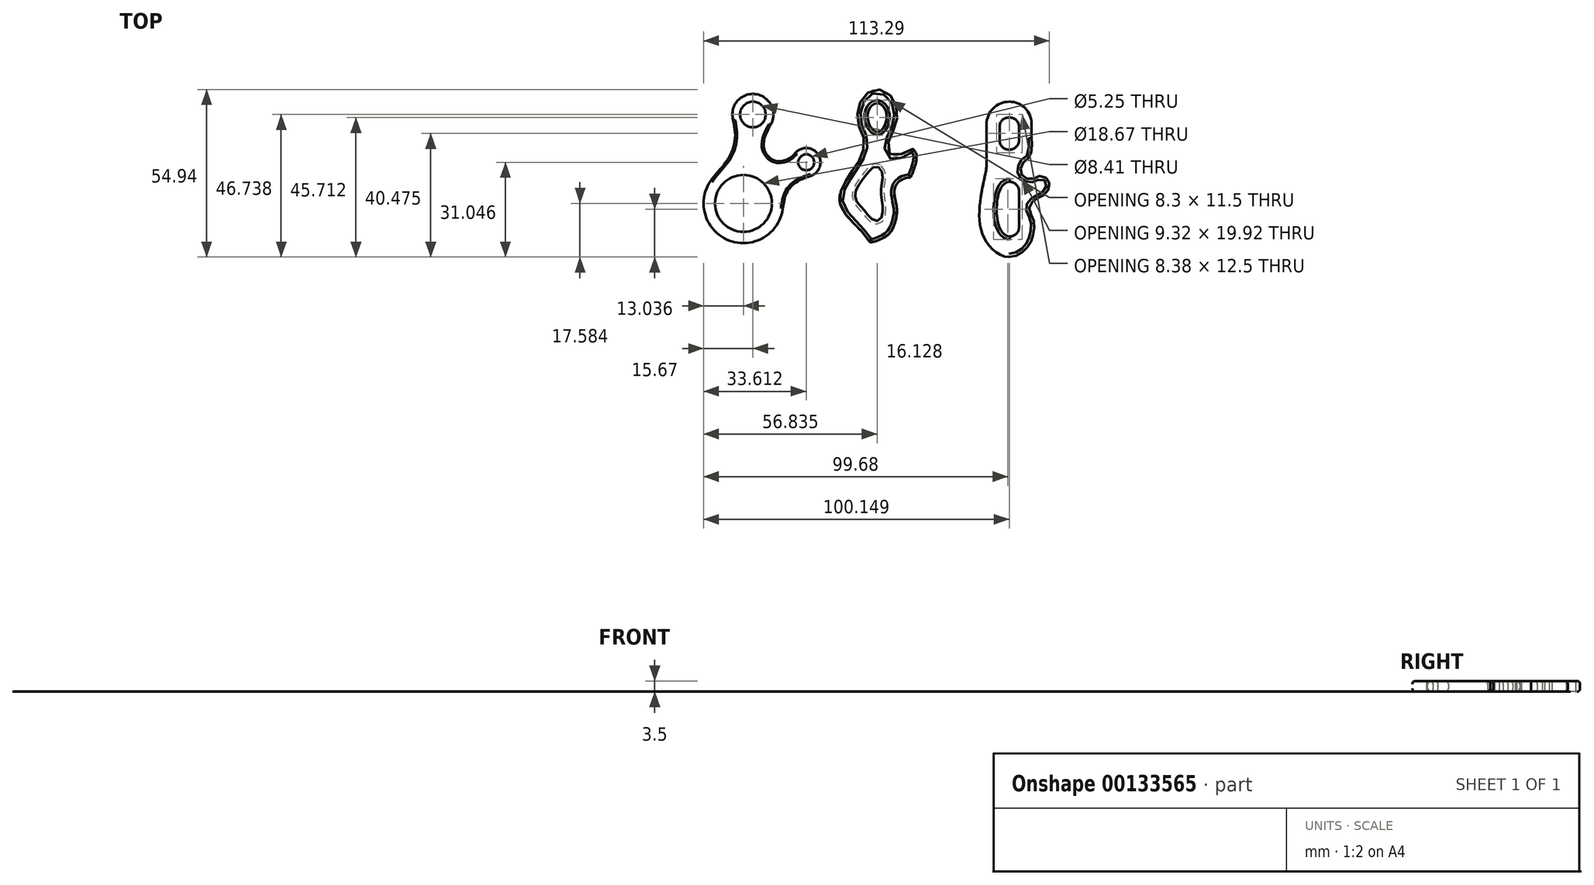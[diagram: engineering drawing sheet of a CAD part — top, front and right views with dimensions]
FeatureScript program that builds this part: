
annotation { "Feature Type Name" : "Feature", "Feature Type Description" : "" }
export const myFeature = defineFeature(function(context is Context, id is Id, definition is map)
    precondition{}
    {
        {
            var Q0;
            Q0=qCreatedBy(makeId("Top.planeOp"),FACE);
            var sketch = newSketch(context, id + "F0", { "sketchPlane" : qUnion([Q0])});
            skCircle(sketch, "E0", {"center": v(-42.03, 15.95) * mm, "radius": 6.72 * mm});
            skPoint(sketch, "E0.first.point", {"position": v(-46.63, 20.85) * mm});
            skPoint(sketch, "E0.second.point", {"position": v(-35.31, 16.12) * mm});
            skPoint(sketch, "E0.third.point", {"position": v(-44.96, 9.9) * mm});
            skCircle(sketch, "E1", {"center": v(-24.55, 0.26) * mm, "radius": 4.69 * mm});
            skPoint(sketch, "E1.first.point", {"position": v(-24.44, 4.94) * mm});
            skPoint(sketch, "E1.second.point", {"position": v(-20.45, -2.01) * mm});
            skPoint(sketch, "E1.third.point", {"position": v(-28.32, -2.52) * mm});
            skCircle(sketch, "E2", {"center": v(-45.12, -13.2) * mm, "radius": 13.03 * mm});
            skPoint(sketch, "E2.first.point", {"position": v(-53.96, -3.63) * mm});
            skPoint(sketch, "E2.second.point", {"position": v(-34.15, -6.18) * mm});
            skPoint(sketch, "E2.third.point", {"position": v(-44.85, -26.24) * mm});
            skFitSpline(sketch, "E3", {"points": [v(-36, 12.97) * mm, v(-38.34, 7.7) * mm, v(-38, 3.62) * mm, v(-34.68, 0.76) * mm, v(-30.27, 1.45) * mm, v(-28, 3.42) * mm], "startDerivative": vector(-12.5, -23.13) * mm, "endDerivative": vector(11.46, 12.78) * mm});
            skFitSpline(sketch, "E4", {"points": [v(-23.1, -4.2) * mm, v(-27.58, -6.11) * mm, v(-30.9, -9.6) * mm, v(-32.22, -15.03) * mm], "startDerivative": vector(-14.25, -4.87) * mm, "endDerivative": vector(-2.28, -16.5) * mm});
            skFitSpline(sketch, "E5", {"points": [v(-48.66, 14.85) * mm, v(-47.85, 8.2) * mm, v(-50.2, 1.33) * mm, v(-55.94, -5.93) * mm], "startDerivative": vector(5.63, -23.91) * mm, "endDerivative": vector(-12.16, -18.24) * mm});
            skCircle(sketch, "E6", {"center": v(-45.12, -13.2) * mm, "radius": 9.34 * mm});
            skCircle(sketch, "E7", {"center": v(-24.55, 0.26) * mm, "radius": 2.63 * mm});
            skCircle(sketch, "E8", {"center": v(-42.03, 15.95) * mm, "radius": 4.2 * mm});
            skSolve(sketch);
        }
        {
            var Q0;
            {var subQ0=sQuery(id+"F0.wireOp",EDGE,"E5");var subQ1=sQuery(id+"F0.wireOp",EDGE,"E0");var subQ2=makeQuery(id+"F0.imprint","INTERSECT",VERTEX,{"disambiguationData":[OD(0.0)],"derivedFrom":[subQ1,subQ0]});Q0=makeQuery(id+"F0.imprint","IMPRINT",FACE,{"disambiguationData":[TD([[makeQuery(id+"F0.imprint","IMPRINT",EDGE,{"disambiguationData":[TD([[subQ2,-1.0]])],"derivedFrom":subQ1}),1.0]])]});}
            var Q1;
            {var subQ0=sQuery(id+"F0.wireOp",EDGE,"E3");var subQ1=sQuery(id+"F0.wireOp",EDGE,"E0");var subQ2=makeQuery(id+"F0.imprint","INTERSECT",VERTEX,{"disambiguationData":[OD(0.0)],"derivedFrom":[subQ1,subQ0]});Q1=makeQuery(id+"F0.imprint","IMPRINT",FACE,{"disambiguationData":[TD([[makeQuery(id+"F0.imprint","IMPRINT",EDGE,{"disambiguationData":[TD([[subQ2,1.0]])],"derivedFrom":subQ1}),1.0]])]});}
            var Q2;
            {var subQ0=sQuery(id+"F0.wireOp",EDGE,"E3");var subQ1=sQuery(id+"F0.wireOp",EDGE,"E1");var subQ2=makeQuery(id+"F0.imprint","INTERSECT",VERTEX,{"disambiguationData":[OD(0.0)],"derivedFrom":[subQ1,subQ0]});Q2=makeQuery(id+"F0.imprint","IMPRINT",FACE,{"disambiguationData":[TD([[makeQuery(id+"F0.imprint","IMPRINT",EDGE,{"disambiguationData":[TD([[subQ2,-1.0]])],"derivedFrom":subQ1}),1.0]])]});}
            var Q3;
            {var subQ0=sQuery(id+"F0.wireOp",EDGE,"E4");var subQ1=sQuery(id+"F0.wireOp",EDGE,"E2");var subQ2=makeQuery(id+"F0.imprint","INTERSECT",VERTEX,{"disambiguationData":[OD(0.0)],"derivedFrom":[subQ1,subQ0]});Q3=makeQuery(id+"F0.imprint","IMPRINT",FACE,{"disambiguationData":[TD([[makeQuery(id+"F0.imprint","IMPRINT",EDGE,{"disambiguationData":[TD([[subQ2,-1.0]])],"derivedFrom":subQ1}),1.0]])]});}
            var Q4;
            Q4=makeQuery(id+"F0.imprint","IMPRINT",FACE,{"disambiguationData":[TD([[makeQuery(id+"F0.imprint","IMPRINT",EDGE,{"derivedFrom":sQuery(id+"F0.wireOp",EDGE,"E7")}),-1.0]])]});
            var Q5;
            Q5=makeQuery(id+"F0.imprint","IMPRINT",FACE,{"disambiguationData":[TD([[makeQuery(id+"F0.imprint","IMPRINT",EDGE,{"derivedFrom":sQuery(id+"F0.wireOp",EDGE,"E6")}),-1.0]])]});
            var Q6;
            Q6=makeQuery(id+"F0.imprint","IMPRINT",FACE,{"disambiguationData":[TD([[makeQuery(id+"F0.imprint","IMPRINT",EDGE,{"derivedFrom":sQuery(id+"F0.wireOp",EDGE,"E8")}),-1.0]])]});
            var Q7;
            {var subQ1=sQuery(id+"F0.wireOp",EDGE,"E0");var subQ5=sQuery(id+"F0.wireOp",EDGE,"E5");var subQ11=makeQuery(id+"F0.imprint","INTERSECT",VERTEX,{"disambiguationData":[OD(1.0)],"derivedFrom":[subQ1,subQ5]});Q7=makeQuery(id+"F0.imprint","IMPRINT",FACE,{"disambiguationData":[TD([[makeQuery(id+"F0.imprint","IMPRINT",EDGE,{"disambiguationData":[TD([[subQ11,-1.0]])],"derivedFrom":subQ1}),-1.0]])]});}
            extrude(context, id + "F1", {"entities" : qUnion([Q0, Q1, Q2, Q3, Q4, Q5, Q6, Q7]), "depth" : 3.5 * mm});
        }
        {
            var Q0;
            Q0=makeQuery(id+"F1.opExtrude","CAP_FACE",FACE,{"disambiguationData":[OSD([sQuery(id+"F0.wireOp",EDGE,"E0"),sQuery(id+"F0.wireOp",EDGE,"E1"),sQuery(id+"F0.wireOp",EDGE,"E2"),sQuery(id+"F0.wireOp",EDGE,"E3"),sQuery(id+"F0.wireOp",EDGE,"E4"),sQuery(id+"F0.wireOp",EDGE,"E5"),sQuery(id+"F0.wireOp",EDGE,"E6"),sQuery(id+"F0.wireOp",EDGE,"E7"),sQuery(id+"F0.wireOp",EDGE,"E8")])],"isStart":false});
            var Q1;
            Q1=makeQuery(id+"F1.opExtrude","CAP_FACE",FACE,{"disambiguationData":[OSD([sQuery(id+"F0.wireOp",EDGE,"E0"),sQuery(id+"F0.wireOp",EDGE,"E1"),sQuery(id+"F0.wireOp",EDGE,"E2"),sQuery(id+"F0.wireOp",EDGE,"E3"),sQuery(id+"F0.wireOp",EDGE,"E4"),sQuery(id+"F0.wireOp",EDGE,"E5"),sQuery(id+"F0.wireOp",EDGE,"E6"),sQuery(id+"F0.wireOp",EDGE,"E7"),sQuery(id+"F0.wireOp",EDGE,"E8")])],"isStart":true});
            fillet(context, id + "F2", {"entities" : qUnion([Q0, Q1]), "radius" : 0.6 * mm, "tangentPropagation" : true, "allowEdgeOverflow" : false});
        }
        {
            var Q0;
            Q0=qCreatedBy(makeId("Top.planeOp"),FACE);
            var sketch = newSketch(context, id + "F3", { "sketchPlane" : qUnion([Q0])});
            skFitSpline(sketch, "E9", {"points": [v(-0.97, 24.13) * mm, v(3.88, 21.07) * mm, v(5.05, 13.74) * mm, v(2.71, 7.82) * mm, v(2.22, 4.17) * mm, v(3.5, 2.34) * mm, v(5.5, 2.26) * mm, v(7.4, 3.58) * mm, v(9.27, 4.44) * mm, v(10.25, 4.56) * mm, v(10.56, 4.56) * mm, v(10.87, 4.13) * mm, v(11.62, 1.8) * mm, v(9.66, -4.56) * mm, v(9.31, -4.67) * mm, v(5.53, -6.23) * mm, v(4.4, -10.79) * mm, v(5.14, -15.04) * mm, v(4.29, -20.3) * mm, v(1.52, -24.07) * mm, v(-2.8, -25.87) * mm, v(-3.7, -25.87) * mm, v(-4.36, -24.9) * mm, v(-7.56, -21.2) * mm, v(-12.04, -16.17) * mm, v(-13.55, -10.95) * mm, v(-10.09, -3.43) * mm, v(-6.7, 1.8) * mm, v(-5.5, 7.28) * mm, v(-6.7, 10.71) * mm, v(-7.8, 15.74) * mm, v(-5.38, 22.2) * mm, v(-0.97, 24.13) * mm]});
            skFitSpline(sketch, "E10", {"points": [v(-1.25, 19.67) * mm, v(1.83, 15.5) * mm, v(-1.2, 10.17) * mm, v(-4.48, 15.7) * mm, v(-1.25, 19.67) * mm]});
            skFitSpline(sketch, "E11", {"points": [v(-0.86, -1.32) * mm, v(0.47, -3.82) * mm, v(0, -8.76) * mm, v(0.5, -16.48) * mm, v(-1.01, -18.93) * mm, v(-3.15, -18.27) * mm, v(-5.57, -15.43) * mm, v(-7.99, -12.58) * mm, v(-8.26, -9) * mm, v(-5.92, -5.26) * mm, v(-3.62, -2.34) * mm, v(-1.9, -1.13) * mm, v(-0.86, -1.32) * mm]});
            skSolve(sketch);
        }
        {
            var Q0;
            Q0=makeQuery(id+"F3.imprint","IMPRINT",FACE,{"disambiguationData":[TD([[makeQuery(id+"F3.imprint","IMPRINT",EDGE,{"derivedFrom":sQuery(id+"F3.wireOp",EDGE,"E9")}),-1.0]])]});
            extrude(context, id + "F4", {"entities" : qUnion([Q0]), "depth" : 3.5 * mm});
        }
        {
            var Q0;
            Q0=makeQuery(id+"F4.opExtrude","CAP_FACE",FACE,{"disambiguationData":[OSD([sQuery(id+"F3.wireOp",EDGE,"E9"),sQuery(id+"F3.wireOp",EDGE,"E10"),sQuery(id+"F3.wireOp",EDGE,"E11")])],"isStart":true});
            var Q1;
            Q1=makeQuery(id+"F4.opExtrude","CAP_FACE",FACE,{"disambiguationData":[OSD([sQuery(id+"F3.wireOp",EDGE,"E9"),sQuery(id+"F3.wireOp",EDGE,"E10"),sQuery(id+"F3.wireOp",EDGE,"E11")])],"isStart":false});
            fillet(context, id + "F5", {"entities" : qUnion([Q0, Q1]), "radius" : 1 * mm, "tangentPropagation" : true, "allowEdgeOverflow" : false});
        }
        {
            var Q0;
            Q0=qCreatedBy(makeId("Top.planeOp"),FACE);
            var sketch = newSketch(context, id + "F6", { "sketchPlane" : qUnion([Q0])});
            skLineSegment(sketch, "E12.bottom", {"start": v(41.8, 14.94) * mm, "end": v(42.18, 14.94) * mm});
            skLineSegment(sketch, "E12.top", {"start": v(41.8, 4.43) * mm, "end": v(42.18, 4.43) * mm});
            skLineSegment(sketch, "E12.left", {"start": v(38.8, 11.94) * mm, "end": v(38.8, 7.43) * mm});
            skLineSegment(sketch, "E12.right", {"start": v(45.18, 11.94) * mm, "end": v(45.18, 7.43) * mm});
            skLineSegment(sketch, "E13.left", {"start": v(45.18, -9.16) * mm, "end": v(45.18, -21.08) * mm});
            skPoint(sketch, "E14.visualSharp", {"position": v(45.18, 14.94) * mm});
            skArc(sketch, "E14.filletArc", {"start": v(45.18, 11.94) * mm, "mid": v(44.3, 14.06) * mm, "end": v(42.18, 14.94) * mm});
            skPoint(sketch, "E15.visualSharp", {"position": v(38.8, 4.43) * mm});
            skArc(sketch, "E15.filletArc", {"start": v(38.8, 7.43) * mm, "mid": v(39.68, 5.31) * mm, "end": v(41.8, 4.43) * mm});
            skPoint(sketch, "E16.visualSharp", {"position": v(38.8, 14.94) * mm});
            skArc(sketch, "E16.filletArc", {"start": v(41.8, 14.94) * mm, "mid": v(39.68, 14.06) * mm, "end": v(38.8, 11.94) * mm});
            skPoint(sketch, "E17.visualSharp", {"position": v(45.18, 4.43) * mm});
            skArc(sketch, "E17.filletArc", {"start": v(42.18, 4.43) * mm, "mid": v(44.3, 5.31) * mm, "end": v(45.18, 7.43) * mm});
            skPoint(sketch, "E18.visualSharp", {"position": v(45.18, -6.16) * mm});
            skArc(sketch, "E18.filletArc", {"start": v(45.18, -9.16) * mm, "mid": v(44.3, -7.04) * mm, "end": v(42.18, -6.16) * mm});
            skPoint(sketch, "E19.visualSharp", {"position": v(45.18, -24.08) * mm});
            skArc(sketch, "E19.filletArc", {"start": v(42.18, -24.08) * mm, "mid": v(44.3, -23.2) * mm, "end": v(45.18, -21.08) * mm});
            skPoint(sketch, "E20.visualSharp", {"position": v(37.86, -24.08) * mm});
            skPoint(sketch, "E21.visualSharp", {"position": v(37.86, -6.16) * mm});
            skFitSpline(sketch, "E22", {"points": [v(42.18, -6.16) * mm, v(40, -7.04) * mm, v(38.37, -10.56) * mm, v(37.86, -15.54) * mm, v(39.15, -21.85) * mm, v(42.18, -24.08) * mm], "startDerivative": vector(-16.44, -0.23) * mm, "endDerivative": vector(17.29, -0.61) * mm});
            skLineSegment(sketch, "E23.bottom", {"start": v(42.03, 20.13) * mm, "end": v(42.13, 20.13) * mm});
            skLineSegment(sketch, "E23.top", {"start": v(41.91, -30.8) * mm, "end": v(41.95, -30.8) * mm});
            skLineSegment(sketch, "E23.left", {"start": v(34.53, 12.63) * mm, "end": v(34.53, -0.55) * mm});
            skLineSegment(sketch, "E23.right", {"start": v(49.27, 12.98) * mm, "end": v(49.27, 8.16) * mm});
            skPoint(sketch, "E24.visualSharp", {"position": v(34.53, 20.13) * mm});
            skArc(sketch, "E24.filletArc", {"start": v(42.03, 20.13) * mm, "mid": v(36.73, 17.93) * mm, "end": v(34.53, 12.63) * mm});
            skPoint(sketch, "E25.visualSharp", {"position": v(49.27, 20.13) * mm});
            skArc(sketch, "E25.filletArc", {"start": v(49.27, 12.98) * mm, "mid": v(47.18, 18.03) * mm, "end": v(42.13, 20.13) * mm});
            skFitSpline(sketch, "E26", {"points": [v(34.53, -0.55) * mm, v(33.88, -4.85) * mm, v(32.17, -17.69) * mm, v(35.4, -27.08) * mm, v(41.95, -30.8) * mm, v(47.75, -27.8) * mm, v(49.9, -23.17) * mm, v(49.95, -18.6) * mm, v(48.85, -16.11) * mm, v(48.8, -13.64) * mm, v(51.5, -11.43) * mm, v(53.92, -9.94) * mm, v(55.1, -7.47) * mm, v(54.31, -5.03) * mm, v(51.86, -4.28) * mm, v(49.27, -5.25) * mm, v(46.37, -4.27) * mm, v(45.71, -1.55) * mm, v(47.31, 0.92) * mm, v(48.85, 2.4) * mm, v(49.27, 8.16) * mm], "startDerivative": vector(0.06, -77.3) * mm, "endDerivative": vector(-6.54, 67.18) * mm});
            skLineSegment(sketch, "E27", {"start": v(49.27, 8.16) * mm, "end": v(49.27, 4.4) * mm});
            skSolve(sketch);
        }
        {
            var Q0;
            Q0=qSketchRegion(id+"F6",true);
            extrude(context, id + "F7", {"entities" : qUnion([Q0]), "depth" : 3.5 * mm});
        }
        {
            var Q0;
            Q0=makeQuery(id+"F7.opExtrude","CAP_FACE",FACE,{"disambiguationData":[OSD([sQuery(id+"F6.wireOp",EDGE,"E12.bottom"),sQuery(id+"F6.wireOp",EDGE,"E12.top"),sQuery(id+"F6.wireOp",EDGE,"E12.left"),sQuery(id+"F6.wireOp",EDGE,"E12.right"),sQuery(id+"F6.wireOp",EDGE,"E13.left"),sQuery(id+"F6.wireOp",EDGE,"E14.filletArc"),sQuery(id+"F6.wireOp",EDGE,"E15.filletArc"),sQuery(id+"F6.wireOp",EDGE,"E16.filletArc"),sQuery(id+"F6.wireOp",EDGE,"E17.filletArc"),sQuery(id+"F6.wireOp",EDGE,"E18.filletArc"),sQuery(id+"F6.wireOp",EDGE,"E19.filletArc"),sQuery(id+"F6.wireOp",EDGE,"E22"),sQuery(id+"F6.wireOp",EDGE,"E23.bottom"),sQuery(id+"F6.wireOp",EDGE,"E23.left"),sQuery(id+"F6.wireOp",EDGE,"E23.right"),sQuery(id+"F6.wireOp",EDGE,"E24.filletArc"),sQuery(id+"F6.wireOp",EDGE,"E25.filletArc"),sQuery(id+"F6.wireOp",EDGE,"E26")])],"isStart":false});
            var Q1;
            Q1=makeQuery(id+"F7.opExtrude","CAP_FACE",FACE,{"disambiguationData":[OSD([sQuery(id+"F6.wireOp",EDGE,"E12.bottom"),sQuery(id+"F6.wireOp",EDGE,"E12.top"),sQuery(id+"F6.wireOp",EDGE,"E12.left"),sQuery(id+"F6.wireOp",EDGE,"E12.right"),sQuery(id+"F6.wireOp",EDGE,"E13.left"),sQuery(id+"F6.wireOp",EDGE,"E14.filletArc"),sQuery(id+"F6.wireOp",EDGE,"E15.filletArc"),sQuery(id+"F6.wireOp",EDGE,"E16.filletArc"),sQuery(id+"F6.wireOp",EDGE,"E17.filletArc"),sQuery(id+"F6.wireOp",EDGE,"E18.filletArc"),sQuery(id+"F6.wireOp",EDGE,"E19.filletArc"),sQuery(id+"F6.wireOp",EDGE,"E22"),sQuery(id+"F6.wireOp",EDGE,"E23.bottom"),sQuery(id+"F6.wireOp",EDGE,"E23.left"),sQuery(id+"F6.wireOp",EDGE,"E23.right"),sQuery(id+"F6.wireOp",EDGE,"E24.filletArc"),sQuery(id+"F6.wireOp",EDGE,"E25.filletArc"),sQuery(id+"F6.wireOp",EDGE,"E26")])],"isStart":true});
            fillet(context, id + "F8", {"entities" : qUnion([Q0, Q1]), "radius" : 1 * mm, "tangentPropagation" : true, "allowEdgeOverflow" : false});
        }
    });
